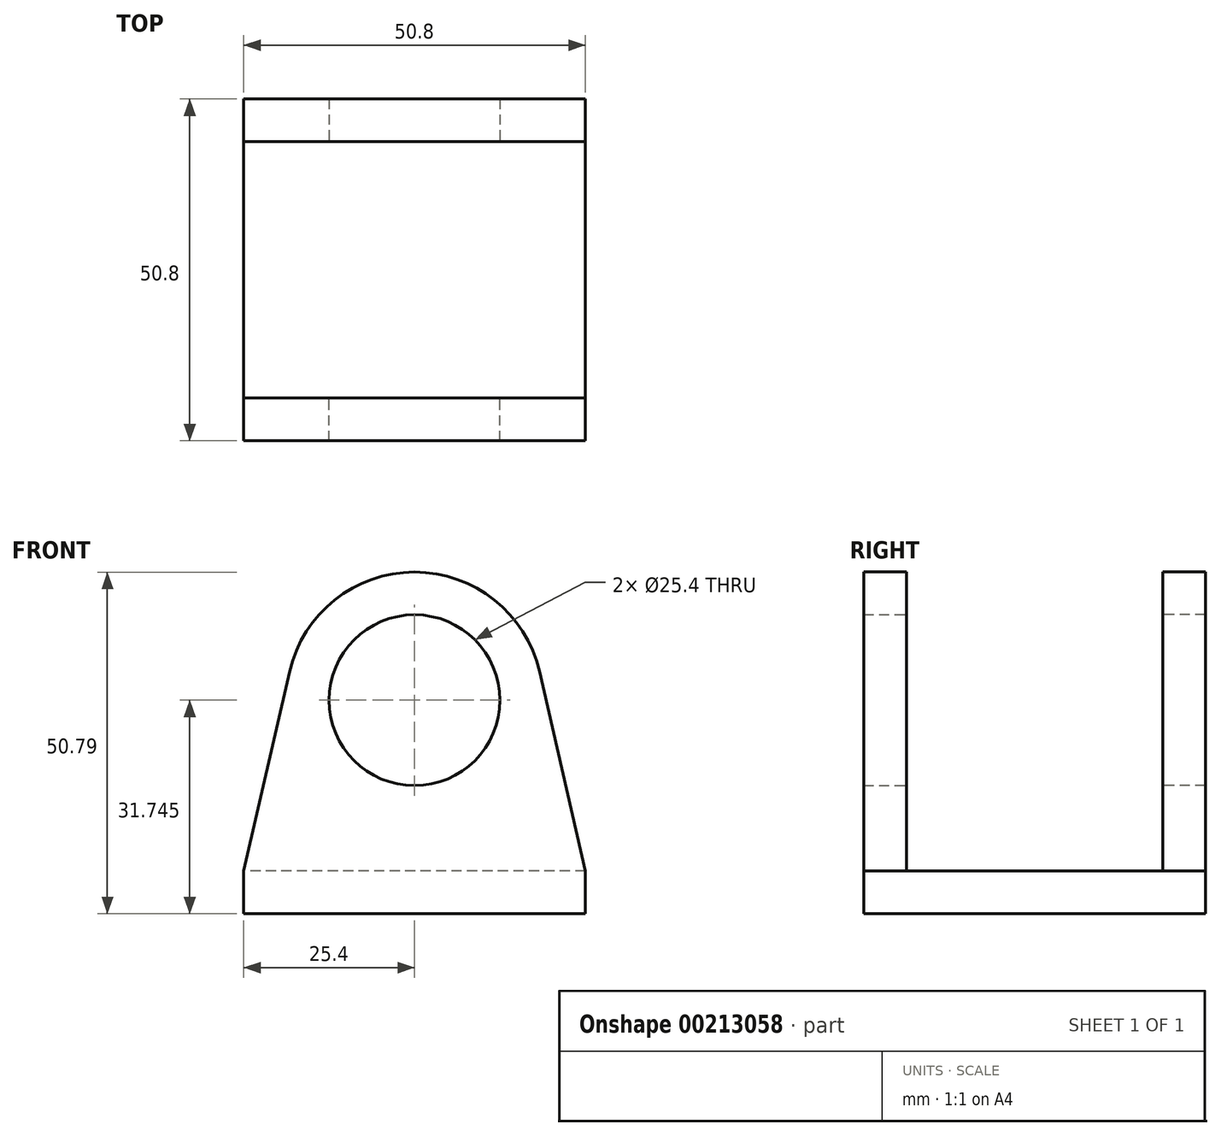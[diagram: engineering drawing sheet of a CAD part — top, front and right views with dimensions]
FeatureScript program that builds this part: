
annotation { "Feature Type Name" : "Feature", "Feature Type Description" : "" }
export const myFeature = defineFeature(function(context is Context, id is Id, definition is map)
    precondition{}
    {
        {
            var Q0;
            Q0=qCreatedBy(makeId("Front.planeOp"),FACE);
            var sketch = newSketch(context, id + "F0", { "sketchPlane" : qUnion([Q0])});
            skLineSegment(sketch, "E0.bottom", {"start": v(25.4, 3.18) * mm, "end": v(-25.4, 3.18) * mm});
            skLineSegment(sketch, "E0.top", {"start": v(25.4, -3.18) * mm, "end": v(-25.4, -3.18) * mm});
            skLineSegment(sketch, "E0.left", {"start": v(25.4, 3.18) * mm, "end": v(25.4, -3.17) * mm});
            skLineSegment(sketch, "E0.right", {"start": v(-25.4, 3.18) * mm, "end": v(-25.4, -3.18) * mm});
            skPoint(sketch, "E0.middle", {"position": v(0, 0) * mm});
            skCircle(sketch, "E1", {"center": v(0, 28.58) * mm, "radius": 12.7 * mm});
            skCircle(sketch, "E2.0", {"center": v(0, 28.58) * mm, "radius": 19.05 * mm});
            skLineSegment(sketch, "E3", {"start": v(-25.4, 3.18) * mm, "end": v(-18.56, 32.85) * mm});
            skLineSegment(sketch, "E4", {"start": v(25.4, 3.18) * mm, "end": v(18.56, 32.85) * mm});
            skSolve(sketch);
        }
        {
            var Q0;
            Q0=makeQuery(id+"F0.imprint","IMPRINT",FACE,{"disambiguationData":[TD([[makeQuery(id+"F0.imprint","IMPRINT",EDGE,{"derivedFrom":sQuery(id+"F0.wireOp",EDGE,"E0.bottom")}),1.0]])]});
            extrude(context, id + "F1", {"entities" : qUnion([Q0]), "depth" : 25.4 * mm});
        }
        {
            var Q0;
            Q0=makeQuery(id+"F0.imprint","IMPRINT",FACE,{"disambiguationData":[TD([[makeQuery(id+"F0.imprint","IMPRINT",EDGE,{"derivedFrom":sQuery(id+"F0.wireOp",EDGE,"E0.bottom")}),-1.0]])]});
            var Q1;
            Q1=makeQuery(id+"F0.imprint","IMPRINT",FACE,{"disambiguationData":[TD([[makeQuery(id+"F0.imprint","IMPRINT",EDGE,{"derivedFrom":sQuery(id+"F0.wireOp",EDGE,"E1")}),-1.0]])]});
            extrude(context, id + "F2", {"entities" : qUnion([Q0, Q1]), "operationType" : NewBodyOperationType.ADD, "depth" : 25.4 * mm, "hasSecondDirection" : true, "secondDirectionOppositeDirection" : false, "secondDirectionDepth" : 19.05 * mm});
        }
        {
            var Q0;
            Q0=makeQuery(id+"F1.opExtrude","SWEPT_BODY",BODY,{"disambiguationData":[OSD([sQuery(id+"F0.wireOp",EDGE,"E0.bottom"),sQuery(id+"F0.wireOp",EDGE,"E0.top"),sQuery(id+"F0.wireOp",EDGE,"E0.left"),sQuery(id+"F0.wireOp",EDGE,"E0.right")])]});
            var Q1;
            Q1=qCreatedBy(makeId("Front.planeOp"),FACE);
            mirror(context, id + "F3", {"operationType" : NewBodyOperationType.ADD, "entities" : qUnion([Q0]), "mirrorPlane" : qUnion([Q1])});
        }
    });
